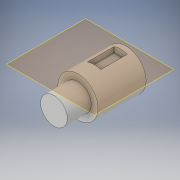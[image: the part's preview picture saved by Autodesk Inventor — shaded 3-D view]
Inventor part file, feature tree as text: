
AUTODESK INVENTOR PART (.ipt)
format: ipt  version: 2019.4 (Build 234330000, 330)  size: 138,752 bytes
history: native  units: mm
features: extrude x3, sketch x3, plane x1, fillet x1
ambient origin geometry x8: Origin, YZ Plane, XZ Plane, XY Plane, X Axis, Y Axis, Z Axis, Center Point
bodies: Body1 (feature_tree)
feature tree (8):
  extrude  "擠出2"  Depth=15.0mm
  extrude  "擠出3"  Depth=18.0mm TaperAngle=0.0deg
  plane  "工作平面2"
  extrude  "擠出6"  Depth=10.0mm
  fillet  "圓角3"  Radius=9.0mm
  sketch  "草圖2"
  sketch  "草圖3"
  sketch  "草圖6"
